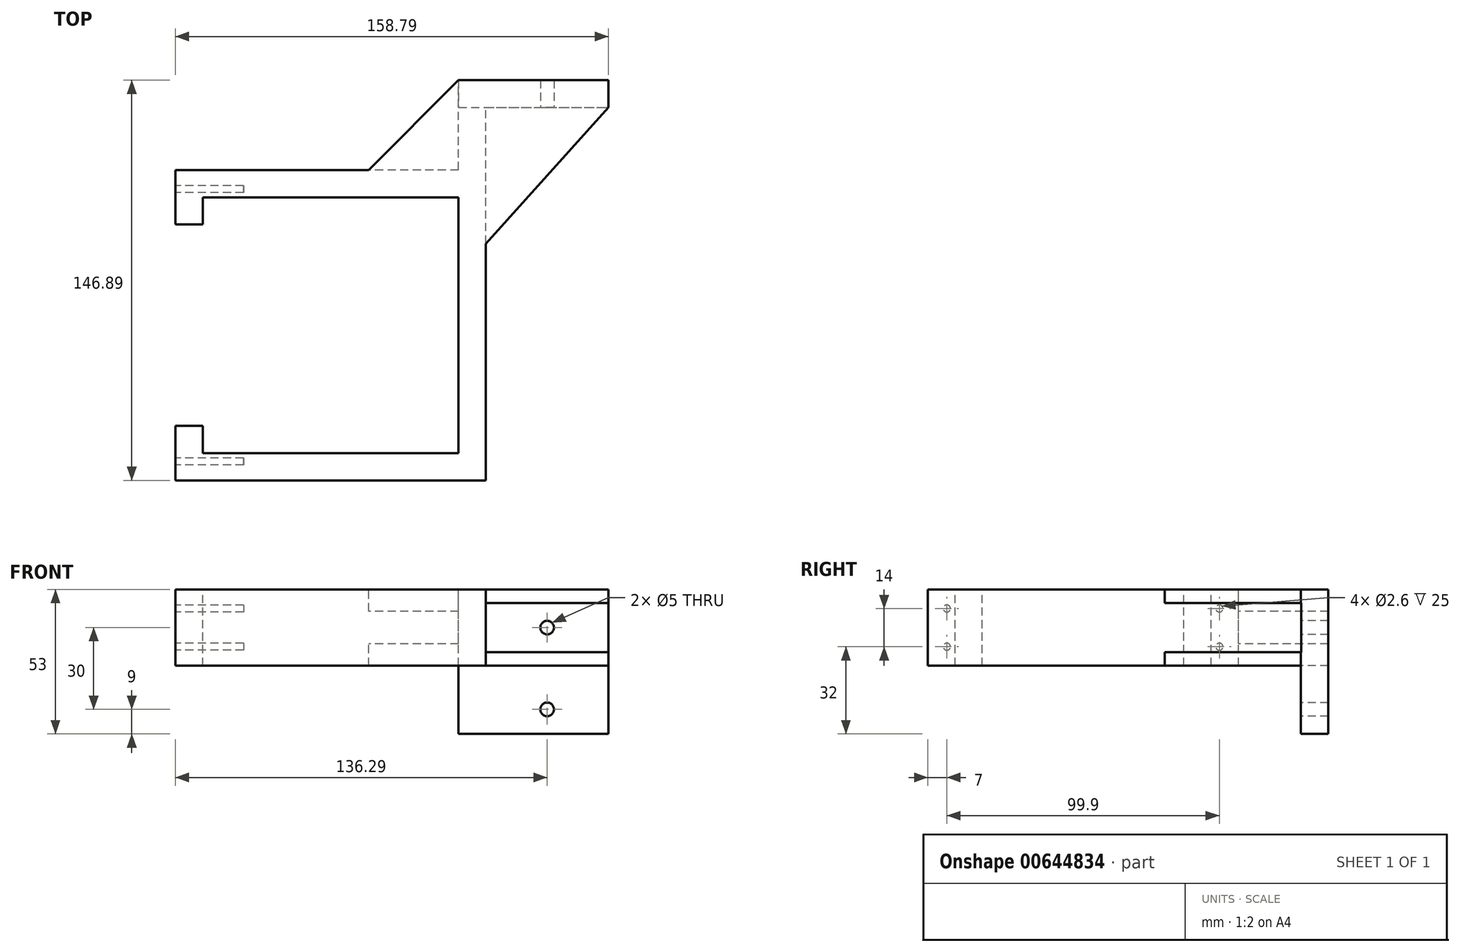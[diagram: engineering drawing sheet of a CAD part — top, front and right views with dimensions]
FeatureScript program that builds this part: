
annotation { "Feature Type Name" : "Feature", "Feature Type Description" : "" }
export const myFeature = defineFeature(function(context is Context, id is Id, definition is map)
    precondition{}
    {
        {
            var Q0;
            Q0=qCreatedBy(makeId("Top.planeOp"),FACE);
            var sketch = newSketch(context, id + "F0", { "sketchPlane" : qUnion([Q0])});
            skLineSegment(sketch, "E0", {"start": v(0, 0) * mm, "end": v(0, 10) * mm});
            skLineSegment(sketch, "E1", {"start": v(0, 10) * mm, "end": v(-10, 10) * mm});
            skLineSegment(sketch, "E2", {"start": v(-10, 10) * mm, "end": v(-10, -10) * mm});
            skLineSegment(sketch, "E3", {"start": v(-10, -10) * mm, "end": v(103.79, -10) * mm});
            skLineSegment(sketch, "E4", {"start": v(103.79, -10) * mm, "end": v(103.79, 126.89) * mm});
            skLineSegment(sketch, "E5", {"start": v(103.8, 126.89) * mm, "end": v(148.79, 126.89) * mm});
            skLineSegment(sketch, "E6", {"start": v(148.79, 126.89) * mm, "end": v(148.79, 136.9) * mm});
            skLineSegment(sketch, "E7", {"start": v(148.79, 136.9) * mm, "end": v(93.8, 136.9) * mm});
            skLineSegment(sketch, "E8", {"start": v(93.8, 136.9) * mm, "end": v(93.8, 103.9) * mm});
            skLineSegment(sketch, "E9", {"start": v(93.8, 103.9) * mm, "end": v(-10, 103.9) * mm});
            skLineSegment(sketch, "E10", {"start": v(-10, 103.9) * mm, "end": v(-10, 83.9) * mm});
            skLineSegment(sketch, "E11", {"start": v(-10, 83.9) * mm, "end": v(0, 83.9) * mm});
            skLineSegment(sketch, "E12", {"start": v(0, 83.9) * mm, "end": v(0, 93.9) * mm});
            skLineSegment(sketch, "E13", {"start": v(0, 93.9) * mm, "end": v(93.8, 93.9) * mm});
            skLineSegment(sketch, "E14", {"start": v(93.8, 93.9) * mm, "end": v(93.8, 0) * mm});
            skLineSegment(sketch, "E15", {"start": v(93.8, 0) * mm, "end": v(0, 0) * mm});
            skSolve(sketch);
        }
        {
            var Q0;
            Q0 = qSketchRegion(id + "F0", true);
            extrude(context, id + "F1", {"entities" : qUnion([Q0]), "oppositeDirection" : true, "depth" : 28 * mm, "offsetDistance" : 25 * mm});
        }
        {
            var Q0;
            Q0=makeQuery(id+"F1.opExtrude","SWEPT_FACE",FACE,{"disambiguationData":[OSD([sQuery(id+"F0.wireOp",EDGE,"E5")])]});
            var sketch = newSketch(context, id + "F2", { "sketchPlane" : qUnion([Q0])});
            skLineSegment(sketch, "E16.bottom", {"start": v(103.79, 0) * mm, "end": v(148.79, 0) * mm});
            skLineSegment(sketch, "E16.top", {"start": v(103.79, -5) * mm, "end": v(148.79, -5) * mm});
            skLineSegment(sketch, "E16.left", {"start": v(103.79, 0) * mm, "end": v(103.79, -5) * mm});
            skLineSegment(sketch, "E16.right", {"start": v(148.79, 0) * mm, "end": v(148.79, -5) * mm});
            skLineSegment(sketch, "E17.bottom", {"start": v(103.79, -28) * mm, "end": v(148.79, -28) * mm});
            skLineSegment(sketch, "E17.top", {"start": v(103.8, -23) * mm, "end": v(148.79, -23) * mm});
            skLineSegment(sketch, "E17.left", {"start": v(103.79, -28) * mm, "end": v(103.79, -23) * mm});
            skLineSegment(sketch, "E17.right", {"start": v(148.79, -28) * mm, "end": v(148.79, -23) * mm});
            skSolve(sketch);
        }
        {
            var Q0;
            Q0 = qSketchRegion(id + "F2", true);
            extrude(context, id + "F3", {"entities" : qUnion([Q0]), "operationType" : NewBodyOperationType.ADD, "depth" : 50 * mm, "offsetDistance" : 25 * mm});
        }
        {
            var Q0;
            Q0=makeQuery(id+"F3.boolean.opBoolean","MERGE",FACE,{"derivedFrom":[makeQuery(id+"F1.opExtrude","CAP_FACE",FACE,{"disambiguationData":[OSD([sQuery(id+"F0.wireOp",EDGE,"E0"),sQuery(id+"F0.wireOp",EDGE,"E1"),sQuery(id+"F0.wireOp",EDGE,"E2"),sQuery(id+"F0.wireOp",EDGE,"E3"),sQuery(id+"F0.wireOp",EDGE,"E4"),sQuery(id+"F0.wireOp",EDGE,"E5"),sQuery(id+"F0.wireOp",EDGE,"E6"),sQuery(id+"F0.wireOp",EDGE,"E7"),sQuery(id+"F0.wireOp",EDGE,"E8"),sQuery(id+"F0.wireOp",EDGE,"E9"),sQuery(id+"F0.wireOp",EDGE,"E10"),sQuery(id+"F0.wireOp",EDGE,"E11"),sQuery(id+"F0.wireOp",EDGE,"E12"),sQuery(id+"F0.wireOp",EDGE,"E13"),sQuery(id+"F0.wireOp",EDGE,"E14"),sQuery(id+"F0.wireOp",EDGE,"E15")])],"isStart":false}),makeQuery(id+"F3.opExtrude","SWEPT_FACE",FACE,{"disambiguationData":[OSD([sQuery(id+"F2.wireOp",EDGE,"E17.bottom")])]})]});
            var sketch = newSketch(context, id + "F4", { "sketchPlane" : qUnion([Q0])});
            skLineSegment(sketch, "E18", {"start": v(103.79, -76.89) * mm, "end": v(148.79, -126.84) * mm});
            skLineSegment(sketch, "E19", {"start": v(148.79, -126.84) * mm, "end": v(148.79, -76.89) * mm});
            skLineSegment(sketch, "E20", {"start": v(148.79, -76.89) * mm, "end": v(105.94, -76.89) * mm});
            skSolve(sketch);
        }
        {
            var Q0;
            {var subQ0=sQuery(id+"F4.wireOp",EDGE,"E18");Q0=makeQuery(id+"F4.imprint","IMPRINT",FACE,{"disambiguationData":[TD([[makeQuery(id+"F4.imprint","IMPRINT",EDGE,{"derivedFrom":subQ0}),1.0]])]});}
            extrude(context, id + "F5", {"entities" : qUnion([Q0]), "operationType" : NewBodyOperationType.REMOVE, "endBound" : BoundingType.THROUGH_ALL, "oppositeDirection" : true, "depth" : 25 * mm, "offsetDistance" : 25 * mm});
        }
        {
            var Q0;
            Q0=makeQuery(id+"F3.boolean.opBoolean","MERGE",FACE,{"derivedFrom":[makeQuery(id+"F1.opExtrude","CAP_FACE",FACE,{"disambiguationData":[OSD([sQuery(id+"F0.wireOp",EDGE,"E0"),sQuery(id+"F0.wireOp",EDGE,"E1"),sQuery(id+"F0.wireOp",EDGE,"E2"),sQuery(id+"F0.wireOp",EDGE,"E3"),sQuery(id+"F0.wireOp",EDGE,"E4"),sQuery(id+"F0.wireOp",EDGE,"E5"),sQuery(id+"F0.wireOp",EDGE,"E6"),sQuery(id+"F0.wireOp",EDGE,"E7"),sQuery(id+"F0.wireOp",EDGE,"E8"),sQuery(id+"F0.wireOp",EDGE,"E9"),sQuery(id+"F0.wireOp",EDGE,"E10"),sQuery(id+"F0.wireOp",EDGE,"E11"),sQuery(id+"F0.wireOp",EDGE,"E12"),sQuery(id+"F0.wireOp",EDGE,"E13"),sQuery(id+"F0.wireOp",EDGE,"E14"),sQuery(id+"F0.wireOp",EDGE,"E15")])],"isStart":true}),makeQuery(id+"F3.opExtrude","SWEPT_FACE",FACE,{"disambiguationData":[OSD([sQuery(id+"F2.wireOp",EDGE,"E16.bottom")])]})]});
            var sketch = newSketch(context, id + "F6", { "sketchPlane" : qUnion([Q0])});
            skLineSegment(sketch, "E21", {"start": v(93.8, 136.9) * mm, "end": v(60.8, 103.9) * mm});
            skSolve(sketch);
        }
        {
            var Q0;
            {var subQ0=sQuery(id+"F6.wireOp",EDGE,"E21");Q0=makeQuery(id+"F6.imprint","IMPRINT",FACE,{"disambiguationData":[TD([[makeQuery(id+"F6.imprint","IMPRINT",EDGE,{"derivedFrom":subQ0}),1.0]])]});}
            extrude(context, id + "F7", {"entities" : qUnion([Q0]), "operationType" : NewBodyOperationType.ADD, "oppositeDirection" : true, "depth" : 28 * mm, "offsetDistance" : 25 * mm});
        }
        {
            var Q0;
            Q0=makeQuery(id+"F1.opExtrude","SWEPT_FACE",FACE,{"disambiguationData":[OSD([sQuery(id+"F0.wireOp",EDGE,"E7")])]});
            var sketch = newSketch(context, id + "F8", { "sketchPlane" : qUnion([Q0])});
            skLineSegment(sketch, "E22.bottom", {"start": v(-93.8, -20) * mm, "end": v(-56.33, -20) * mm});
            skLineSegment(sketch, "E22.top", {"start": v(-93.8, -8) * mm, "end": v(-56.33, -8) * mm});
            skLineSegment(sketch, "E22.left", {"start": v(-93.8, -20) * mm, "end": v(-93.8, -8) * mm});
            skLineSegment(sketch, "E22.right", {"start": v(-56.33, -20) * mm, "end": v(-56.33, -8) * mm});
            skSolve(sketch);
        }
        {
            var Q0;
            Q0=makeQuery(id+"F8.imprint","IMPRINT",FACE,{"disambiguationData":[TD([[makeQuery(id+"F8.imprint","IMPRINT",EDGE,{"derivedFrom":sQuery(id+"F8.wireOp",EDGE,"E22.bottom")}),1.0]])]});
            extrude(context, id + "F9", {"entities" : qUnion([Q0]), "operationType" : NewBodyOperationType.REMOVE, "oppositeDirection" : true, "depth" : 33 * mm, "offsetDistance" : 25 * mm});
        }
        {
            var Q0;
            {var subQ0=sQuery(id+"F0.wireOp",EDGE,"E9");var subQ1=sQuery(id+"F0.wireOp",EDGE,"E8");Q0=makeQuery(id+"F7.boolean.opBoolean","MERGE",FACE,{"derivedFrom":[makeQuery(id+"F3.boolean.opBoolean","MERGE",FACE,{"derivedFrom":[makeQuery(id+"F1.opExtrude","CAP_FACE",FACE,{"disambiguationData":[OSD([sQuery(id+"F0.wireOp",EDGE,"E0"),sQuery(id+"F0.wireOp",EDGE,"E1"),sQuery(id+"F0.wireOp",EDGE,"E2"),sQuery(id+"F0.wireOp",EDGE,"E3"),sQuery(id+"F0.wireOp",EDGE,"E4"),sQuery(id+"F0.wireOp",EDGE,"E5"),sQuery(id+"F0.wireOp",EDGE,"E6"),sQuery(id+"F0.wireOp",EDGE,"E7"),subQ1,subQ0,sQuery(id+"F0.wireOp",EDGE,"E10"),sQuery(id+"F0.wireOp",EDGE,"E11"),sQuery(id+"F0.wireOp",EDGE,"E12"),sQuery(id+"F0.wireOp",EDGE,"E13"),sQuery(id+"F0.wireOp",EDGE,"E14"),sQuery(id+"F0.wireOp",EDGE,"E15")])],"isStart":false}),makeQuery(id+"F3.opExtrude","SWEPT_FACE",FACE,{"disambiguationData":[OSD([sQuery(id+"F2.wireOp",EDGE,"E17.bottom")])]})]}),makeQuery(id+"F7.opExtrude","CAP_FACE",FACE,{"disambiguationData":[OSD([subQ1,subQ0,sQuery(id+"F6.wireOp",EDGE,"E21")])],"isStart":false})]});}
            var sketch = newSketch(context, id + "F10", { "sketchPlane" : qUnion([Q0])});
            skLineSegment(sketch, "E23", {"start": v(148.79, -136.9) * mm, "end": v(93.8, -136.9) * mm});
            skLineSegment(sketch, "E24", {"start": v(93.8, -136.9) * mm, "end": v(93.8, -126.84) * mm});
            skLineSegment(sketch, "E25", {"start": v(93.8, -126.84) * mm, "end": v(148.79, -126.84) * mm});
            skSolve(sketch);
        }
        {
            var Q0;
            Q0=makeQuery(id+"F10.imprint","IMPRINT",FACE,{"disambiguationData":[TD([[makeQuery(id+"F10.imprint","IMPRINT",EDGE,{"derivedFrom":sQuery(id+"F10.wireOp",EDGE,"E23")}),-1.0]])]});
            extrude(context, id + "F11", {"entities" : qUnion([Q0]), "operationType" : NewBodyOperationType.ADD, "depth" : 25 * mm, "offsetDistance" : 25 * mm});
        }
        {
            var Q0;
            Q0=makeQuery(id+"F11.opExtrude","SWEPT_FACE",FACE,{"disambiguationData":[OSD([sQuery(id+"F10.wireOp",EDGE,"E25")])]});
            var sketch = newSketch(context, id + "F12", { "sketchPlane" : qUnion([Q0])});
            skCircle(sketch, "E26", {"center": v(126.3, -44) * mm, "radius": 2.5 * mm});
            skCircle(sketch, "E27", {"center": v(126.3, -14) * mm, "radius": 2.5 * mm});
            skSolve(sketch);
        }
        {
            var Q0;
            Q0=makeQuery(id+"F12.imprint","IMPRINT",FACE,{"disambiguationData":[TD([[makeQuery(id+"F12.imprint","IMPRINT",EDGE,{"derivedFrom":sQuery(id+"F12.wireOp",EDGE,"E27")}),1.0]])]});
            var Q1;
            Q1=makeQuery(id+"F12.imprint","IMPRINT",FACE,{"disambiguationData":[TD([[makeQuery(id+"F12.imprint","IMPRINT",EDGE,{"derivedFrom":sQuery(id+"F12.wireOp",EDGE,"E26")}),1.0]])]});
            extrude(context, id + "F13", {"entities" : qUnion([Q0, Q1]), "operationType" : NewBodyOperationType.REMOVE, "endBound" : BoundingType.THROUGH_ALL, "oppositeDirection" : true, "depth" : 25 * mm, "offsetDistance" : 25 * mm});
        }
        {
            var Q0;
            Q0=makeQuery(id+"F1.opExtrude","SWEPT_FACE",FACE,{"disambiguationData":[OSD([sQuery(id+"F0.wireOp",EDGE,"E10")])]});
            var sketch = newSketch(context, id + "F14", { "sketchPlane" : qUnion([Q0])});
            skCircle(sketch, "E28", {"center": v(-96.9, -7) * mm, "radius": 1.3 * mm});
            skCircle(sketch, "E29", {"center": v(-96.9, -21) * mm, "radius": 1.3 * mm});
            skCircle(sketch, "E30", {"center": v(3, -7) * mm, "radius": 1.3 * mm});
            skCircle(sketch, "E31", {"center": v(3, -21) * mm, "radius": 1.3 * mm});
            skSolve(sketch);
        }
        {
            var Q0;
            Q0=makeQuery(id+"F14.imprint","IMPRINT",FACE,{"disambiguationData":[TD([[makeQuery(id+"F14.imprint","IMPRINT",EDGE,{"derivedFrom":sQuery(id+"F14.wireOp",EDGE,"E28")}),1.0]])]});
            var Q1;
            Q1=makeQuery(id+"F14.imprint","IMPRINT",FACE,{"disambiguationData":[TD([[makeQuery(id+"F14.imprint","IMPRINT",EDGE,{"derivedFrom":sQuery(id+"F14.wireOp",EDGE,"E29")}),1.0]])]});
            var Q2;
            Q2=makeQuery(id+"F14.imprint","IMPRINT",FACE,{"disambiguationData":[TD([[makeQuery(id+"F14.imprint","IMPRINT",EDGE,{"derivedFrom":sQuery(id+"F14.wireOp",EDGE,"E30")}),1.0]])]});
            var Q3;
            Q3=makeQuery(id+"F14.imprint","IMPRINT",FACE,{"disambiguationData":[TD([[makeQuery(id+"F14.imprint","IMPRINT",EDGE,{"derivedFrom":sQuery(id+"F14.wireOp",EDGE,"E31")}),1.0]])]});
            extrude(context, id + "F15", {"entities" : qUnion([Q0, Q1, Q2, Q3]), "operationType" : NewBodyOperationType.REMOVE, "oppositeDirection" : true, "depth" : 25 * mm, "offsetDistance" : 25 * mm});
        }
    });
